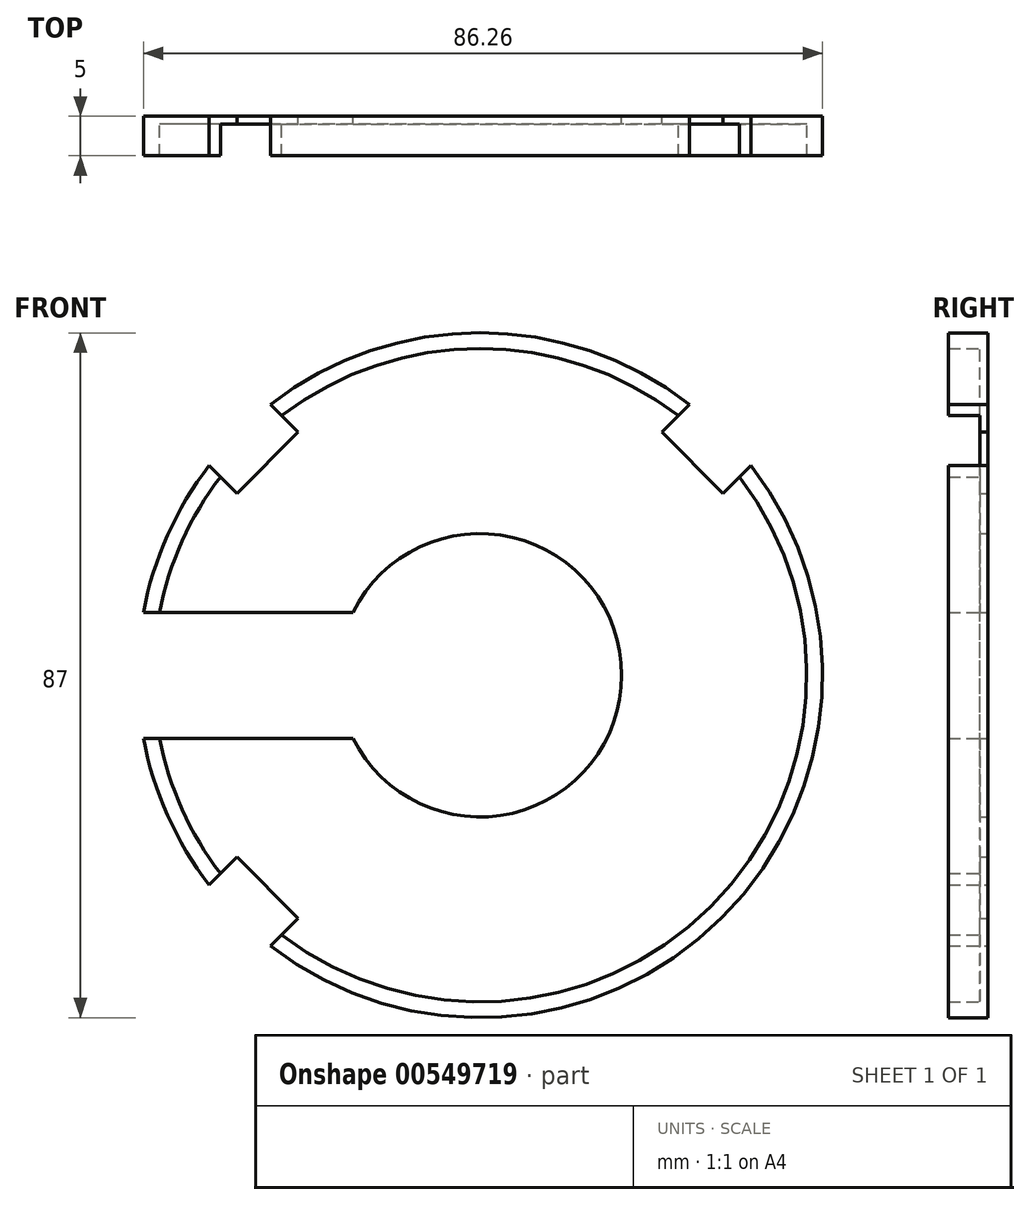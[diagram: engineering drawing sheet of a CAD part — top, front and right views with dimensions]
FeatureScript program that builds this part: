
annotation { "Feature Type Name" : "Feature", "Feature Type Description" : "" }
export const myFeature = defineFeature(function(context is Context, id is Id, definition is map)
    precondition{}
    {
        {
            var Q0;
            Q0=qCreatedBy(makeId("Front.planeOp"),FACE);
            var sketch = newSketch(context, id + "F0", { "sketchPlane" : qUnion([Q0])});
            skArc(sketch, "E0", {"start": v(-40.72, -8) * mm, "mid": v(41.5, 0) * mm, "end": v(-40.72, 8) * mm});
            skArc(sketch, "E1", {"start": v(-16.12, -8) * mm, "mid": v(18, 0) * mm, "end": v(-16.12, 8) * mm});
            skLineSegment(sketch, "E2", {"start": v(-16.12, 8) * mm, "end": v(-40.72, 8) * mm});
            skLineSegment(sketch, "E3", {"start": v(-16.12, -8) * mm, "end": v(-40.72, -8) * mm});
            skSolve(sketch);
        }
        {
            var Q0;
            Q0=makeQuery(id+"F0.imprint","IMPRINT",FACE,{"disambiguationData":[TD([[makeQuery(id+"F0.imprint","IMPRINT",EDGE,{"derivedFrom":sQuery(id+"F0.wireOp",EDGE,"E0")}),1.0]])]});
            extrude(context, id + "F1", {"entities" : qUnion([Q0]), "depth" : 1 * mm, "offsetDistance" : 25 * mm});
        }
        {
            var Q0;
            Q0=makeQuery(id+"F1.opExtrude","CAP_FACE",FACE,{"disambiguationData":[OSD([sQuery(id+"F0.wireOp",EDGE,"E0"),sQuery(id+"F0.wireOp",EDGE,"E1"),sQuery(id+"F0.wireOp",EDGE,"E2"),sQuery(id+"F0.wireOp",EDGE,"E3")])],"isStart":true});
            var sketch = newSketch(context, id + "F2", { "sketchPlane" : qUnion([Q0])});
            skArc(sketch, "E4", {"start": v(42.76, 8) * mm, "mid": v(-43.5, 0) * mm, "end": v(42.76, -8) * mm});
            skArc(sketch, "E5", {"start": v(40.72, 8) * mm, "mid": v(-41.5, 0) * mm, "end": v(40.72, -8) * mm});
            skLineSegment(sketch, "E6", {"start": v(40.72, 8) * mm, "end": v(42.76, 8) * mm});
            skLineSegment(sketch, "E7", {"start": v(40.72, -8) * mm, "end": v(42.76, -8) * mm});
            skSolve(sketch);
        }
        {
            var Q0;
            Q0 = qSketchRegion(id + "F2", true);
            extrude(context, id + "F3", {"entities" : qUnion([Q0]), "operationType" : NewBodyOperationType.ADD, "oppositeDirection" : true, "depth" : 5 * mm, "offsetDistance" : 25 * mm});
        }
        {
            var Q0;
            Q0=makeQuery(id+"F2.imprint","IMPRINT",FACE,{"disambiguationData":[TD([[makeQuery(id+"F2.imprint","IMPRINT",EDGE,{"derivedFrom":sQuery(id+"F2.wireOp",EDGE,"E5")}),-1.0]])]});
            var sketch = newSketch(context, id + "F4", { "sketchPlane" : qUnion([Q0])});
            skLineSegment(sketch, "E8", {"start": v(0, 53.26) * mm, "end": v(0, -53.42) * mm, "construction": true});
            skLineSegment(sketch, "E9", {"start": v(53.95, -53.95) * mm, "end": v(-47.93, 47.93) * mm, "construction": true});
            skLineSegment(sketch, "E10", {"start": v(23.09, -30.87) * mm, "end": v(26.62, -34.4) * mm});
            skLineSegment(sketch, "E11", {"start": v(30.87, -23.09) * mm, "end": v(34.4, -26.62) * mm});
            skLineSegment(sketch, "E12", {"start": v(23.09, -30.87) * mm, "end": v(30.87, -23.09) * mm});
            skPoint(sketch, "E13.orphan", {"position": v(42.76, -8) * mm});
            skArc(sketch, "E14.trimOffspring", {"start": v(26.62, -34.4) * mm, "mid": v(30.76, -30.76) * mm, "end": v(34.4, -26.62) * mm});
            skPoint(sketch, "E15.orphan", {"position": v(42.76, 8) * mm});
            skLineSegment(sketch, "E16.1.0", {"start": v(23.09, 30.87) * mm, "end": v(26.62, 34.4) * mm});
            skLineSegment(sketch, "E16.1.1", {"start": v(30.87, 23.09) * mm, "end": v(23.09, 30.87) * mm});
            skLineSegment(sketch, "E16.1.2", {"start": v(30.87, 23.09) * mm, "end": v(34.4, 26.62) * mm});
            skArc(sketch, "E16.1.3", {"start": v(34.4, 26.62) * mm, "mid": v(30.76, 30.76) * mm, "end": v(26.62, 34.4) * mm});
            skLineSegment(sketch, "E16.2.0", {"start": v(-30.87, 23.09) * mm, "end": v(-34.4, 26.62) * mm});
            skLineSegment(sketch, "E16.2.1", {"start": v(-23.09, 30.87) * mm, "end": v(-30.87, 23.09) * mm});
            skLineSegment(sketch, "E16.2.2", {"start": v(-23.09, 30.87) * mm, "end": v(-26.62, 34.4) * mm});
            skArc(sketch, "E16.2.3", {"start": v(-26.62, 34.4) * mm, "mid": v(-30.76, 30.76) * mm, "end": v(-34.4, 26.62) * mm});
            skLineSegment(sketch, "E16.anchor1", {"start": v(0, 0) * mm, "end": v(34.4, -26.62) * mm, "construction": true});
            skLineSegment(sketch, "E16.anchor2", {"start": v(0, 0) * mm, "end": v(-34.4, 26.62) * mm, "construction": true});
            skSolve(sketch);
        }
        {
            var Q0;
            Q0 = qSketchRegion(id + "F4", true);
            var Q1;
            Q1=makeQuery(id+"F3.opExtrude","CAP_FACE",FACE,{"disambiguationData":[OSD([sQuery(id+"F2.wireOp",EDGE,"E4"),sQuery(id+"F2.wireOp",EDGE,"E5"),sQuery(id+"F2.wireOp",EDGE,"E6"),sQuery(id+"F2.wireOp",EDGE,"E7")])],"isStart":false});
            extrude(context, id + "F5", {"entities" : qUnion([Q0]), "operationType" : NewBodyOperationType.REMOVE, "endBound" : BoundingType.UP_TO_SURFACE, "oppositeDirection" : true, "depth" : 25 * mm, "endBoundEntityFace" : qUnion([Q1]), "offsetDistance" : 25 * mm});
        }
    });
